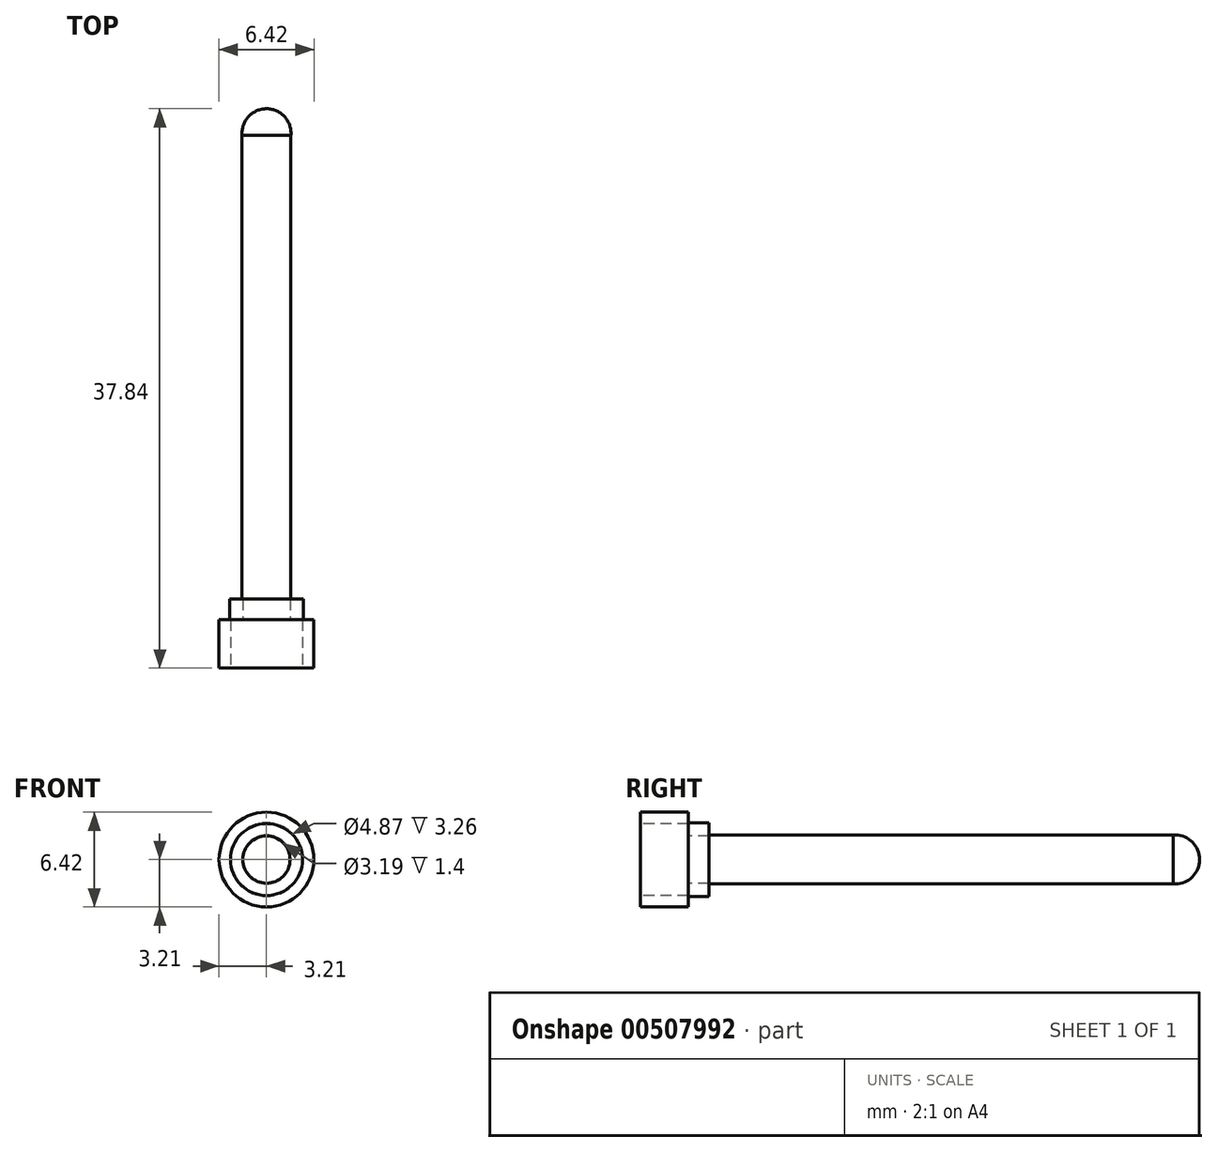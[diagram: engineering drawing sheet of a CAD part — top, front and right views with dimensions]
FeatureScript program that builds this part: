
annotation { "Feature Type Name" : "Feature", "Feature Type Description" : "" }
export const myFeature = defineFeature(function(context is Context, id is Id, definition is map)
    precondition{}
    {
        {
            var Q0;
            Q0=qCreatedBy(makeId("Front.planeOp"),FACE);
            var sketch = newSketch(context, id + "F0", { "sketchPlane" : qUnion([Q0])});
            skCircle(sketch, "E0", {"center": v(0, 0) * mm, "radius": 3.2 * mm});
            skCircle(sketch, "E1", {"center": v(0, 0) * mm, "radius": 2.44 * mm});
            skSolve(sketch);
        }
        {
            var Q0;
            Q0 = qSketchRegion(id + "F0", true);
            extrude(context, id + "F1", {"entities" : qUnion([Q0]), "oppositeDirection" : true, "depth" : 3.26 * mm, "offsetDistance" : 25 * mm});
        }
        {
            var Q0;
            Q0=makeQuery(id+"F1.opExtrude","CAP_FACE",FACE,{"disambiguationData":[OSD([sQuery(id+"F0.wireOp",EDGE,"E0"),sQuery(id+"F0.wireOp",EDGE,"E1")])],"isStart":false});
            var sketch = newSketch(context, id + "F2", { "sketchPlane" : qUnion([Q0])});
            skCircle(sketch, "E2", {"center": v(0, 0) * mm, "radius": 2.5 * mm});
            skCircle(sketch, "E3", {"center": v(0, 0) * mm, "radius": 1.6 * mm});
            skSolve(sketch);
        }
        {
            var Q0;
            Q0 = qSketchRegion(id + "F2", true);
            extrude(context, id + "F3", {"entities" : qUnion([Q0]), "operationType" : NewBodyOperationType.ADD, "depth" : 1.4 * mm, "offsetDistance" : 25 * mm});
        }
        {
            var Q0;
            Q0=makeQuery(id+"F3.opExtrude","CAP_FACE",FACE,{"disambiguationData":[OSD([sQuery(id+"F2.wireOp",EDGE,"E2"),sQuery(id+"F2.wireOp",EDGE,"E3")])],"isStart":false});
            var sketch = newSketch(context, id + "F4", { "sketchPlane" : qUnion([Q0])});
            skCircle(sketch, "E4", {"center": v(0, 0) * mm, "radius": 1.65 * mm});
            skSolve(sketch);
        }
        {
            var Q0;
            Q0 = qSketchRegion(id + "F4", true);
            extrude(context, id + "F5", {"entities" : qUnion([Q0]), "operationType" : NewBodyOperationType.ADD, "depth" : 31.52 * mm, "offsetDistance" : 25 * mm});
        }
        {
            var Q0;
            Q0=makeQuery(id+"F5.opExtrude","CAP_FACE",FACE,{"disambiguationData":[OSD([sQuery(id+"F4.wireOp",EDGE,"E4")])],"isStart":false});
            var sketch = newSketch(context, id + "F6", { "sketchPlane" : qUnion([Q0])});
            skCircle(sketch, "E5", {"center": v(0, 0) * mm, "radius": 1.65 * mm});
            skSolve(sketch);
        }
        {
            var Q0;
            Q0=makeQuery(id+"F6.imprint","IMPRINT",FACE,{"disambiguationData":[TD([[makeQuery(id+"F6.imprint","IMPRINT",EDGE,{"derivedFrom":sQuery(id+"F6.wireOp",EDGE,"E5")}),1.0]])]});
            var sketch = newSketch(context, id + "F7", { "sketchPlane" : qUnion([Q0])});
            skArc(sketch, "E6", {"start": v(0, -1.66) * mm, "mid": v(1.66, 0) * mm, "end": v(0, 1.66) * mm});
            skLineSegment(sketch, "E7", {"start": v(0, 1.66) * mm, "end": v(0, -1.66) * mm});
            skSolve(sketch);
        }
        {
            var Q0;
            Q0 = qSketchRegion(id + "F7", true);
            var Q1;
            Q1=sQuery(id+"F7.wireOp",EDGE,"E7");
            revolve(context, id + "F8", {"operationType" : NewBodyOperationType.ADD, "entities" : qUnion([Q0]), "axis" : qUnion([Q1]), "revolveType" : RevolveType.FULL});
        }
    });
